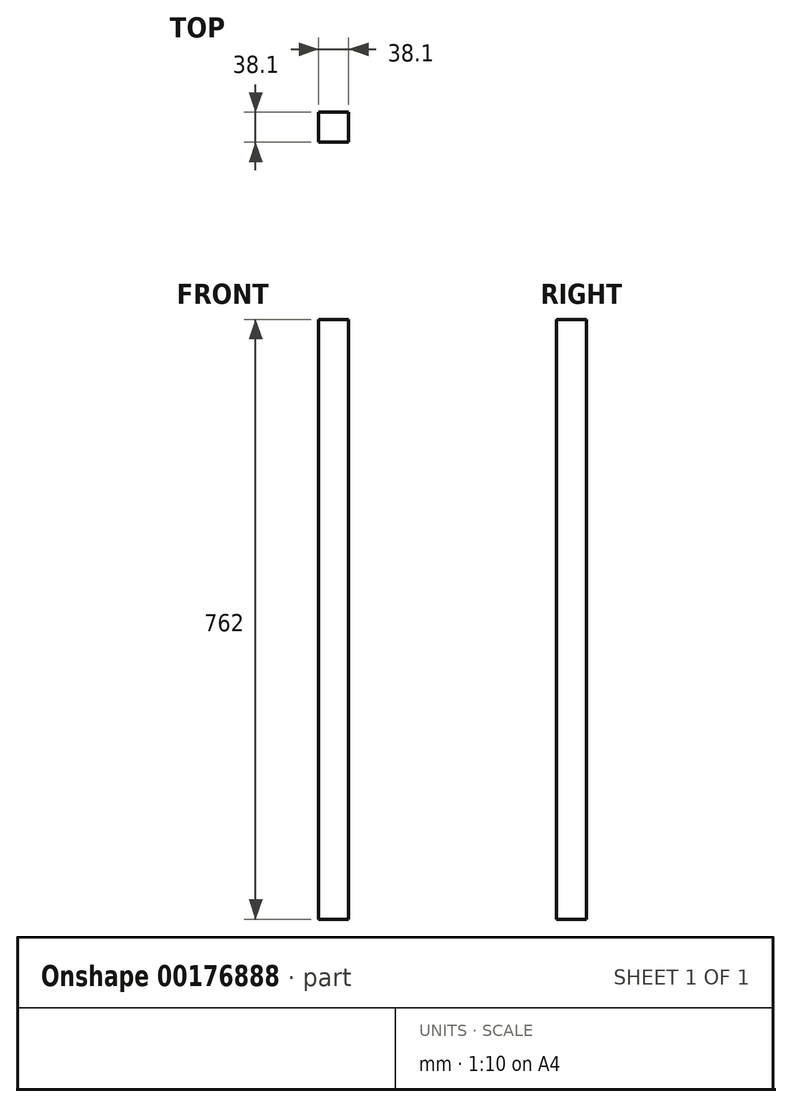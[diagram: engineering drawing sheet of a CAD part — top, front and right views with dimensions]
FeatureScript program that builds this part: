
annotation { "Feature Type Name" : "Feature", "Feature Type Description" : "" }
export const myFeature = defineFeature(function(context is Context, id is Id, definition is map)
    precondition{}
    {
        {
            var Q0;
            Q0=qCreatedBy(makeId("Front.planeOp"),FACE);
            var sketch = newSketch(context, id + "F0", { "sketchPlane" : qUnion([Q0])});
            skLineSegment(sketch, "E0.bottom", {"start": v(-19.05, 381) * mm, "end": v(19.05, 381) * mm});
            skLineSegment(sketch, "E0.top", {"start": v(-19.05, -381) * mm, "end": v(19.05, -381) * mm});
            skLineSegment(sketch, "E0.left", {"start": v(-19.05, 381) * mm, "end": v(-19.05, -381) * mm});
            skLineSegment(sketch, "E0.right", {"start": v(19.05, 381) * mm, "end": v(19.05, -381) * mm});
            skPoint(sketch, "E0.middle", {"position": v(0, 0) * mm});
            skSolve(sketch);
        }
        {
            var Q0;
            Q0 = qSketchRegion(id + "F0", true);
            extrude(context, id + "F1", {"entities" : qUnion([Q0]), "depth" : 38.1 * mm});
        }
    });
